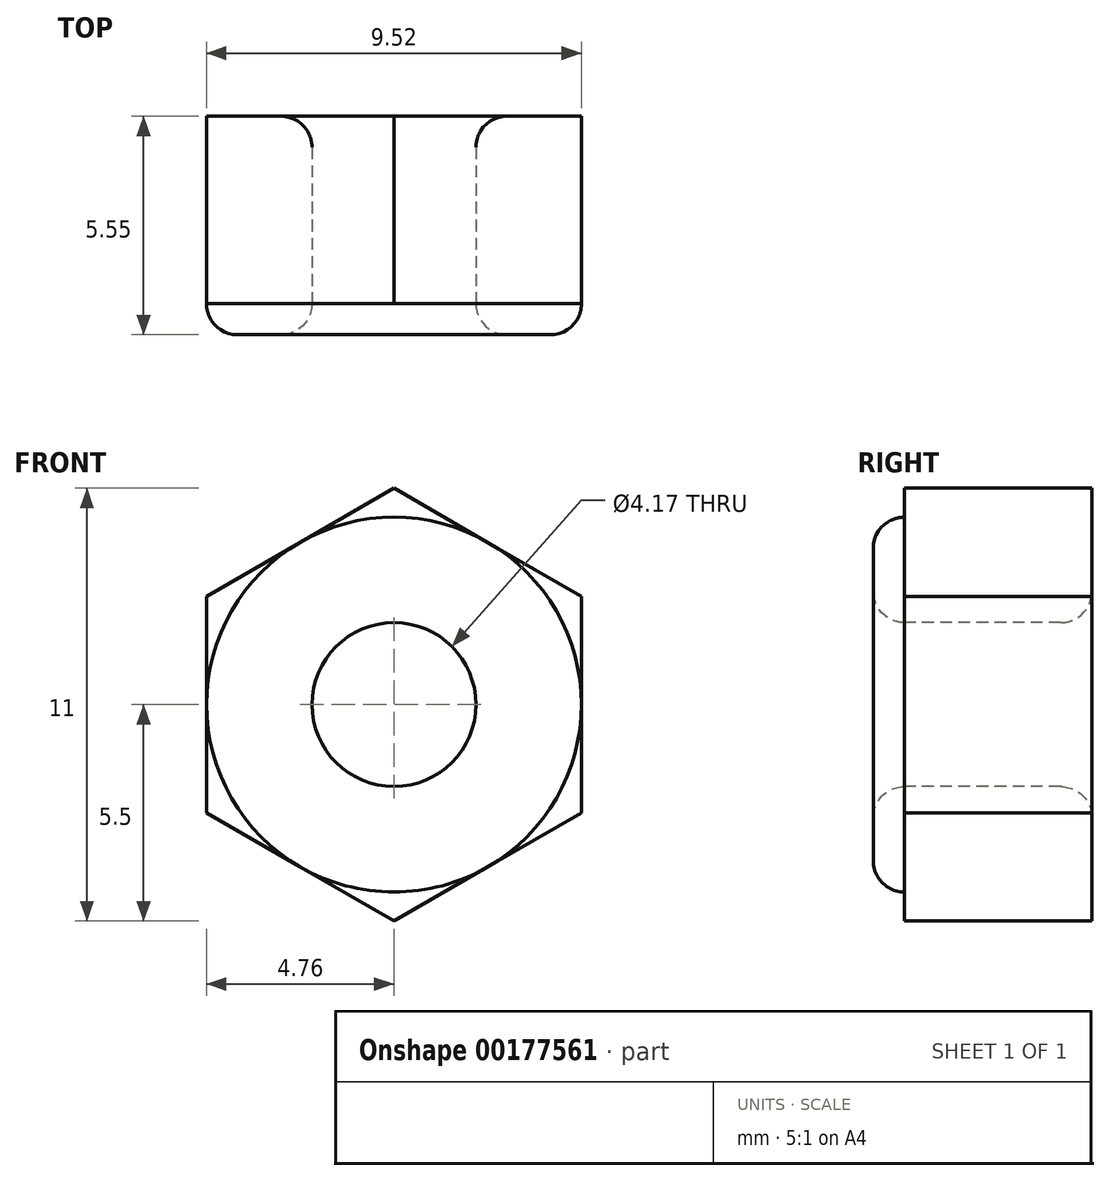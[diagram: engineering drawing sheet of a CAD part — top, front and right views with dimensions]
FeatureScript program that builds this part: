
annotation { "Feature Type Name" : "Feature", "Feature Type Description" : "" }
export const myFeature = defineFeature(function(context is Context, id is Id, definition is map)
    precondition{}
    {
        {
            var Q0;
            Q0=qCreatedBy(makeId("Front.planeOp"),FACE);
            var sketch = newSketch(context, id + "F0", { "sketchPlane" : qUnion([Q0])});
            skCircle(sketch, "E0.cCircle", {"center": v(0, 0) * mm, "radius": 4.76 * mm, "construction": true});
            skLineSegment(sketch, "E0.0", {"start": v(4.76, 2.75) * mm, "end": v(4.76, -2.75) * mm});
            skLineSegment(sketch, "E0.1", {"start": v(4.76, -2.75) * mm, "end": v(0, -5.5) * mm});
            skLineSegment(sketch, "E0.2", {"start": v(0, -5.5) * mm, "end": v(-4.76, -2.75) * mm});
            skLineSegment(sketch, "E0.3", {"start": v(-4.76, -2.75) * mm, "end": v(-4.76, 2.75) * mm});
            skLineSegment(sketch, "E0.4", {"start": v(-4.76, 2.75) * mm, "end": v(0, 5.5) * mm});
            skLineSegment(sketch, "E0.5", {"start": v(0, 5.5) * mm, "end": v(4.76, 2.75) * mm});
            skPoint(sketch, "E0.0.midPoint", {"position": v(4.76, 0) * mm});
            skCircle(sketch, "E1", {"center": v(0, 0) * mm, "radius": 2.08 * mm});
            skSolve(sketch);
        }
        {
            var Q0;
            Q0 = qSketchRegion(id + "F0", true);
            extrude(context, id + "F1", {"entities" : qUnion([Q0]), "oppositeDirection" : true, "depth" : 4.76 * mm});
        }
        {
            var Q0;
            Q0=makeQuery(id+"F1.opExtrude","CAP_FACE",FACE,{"disambiguationData":[OSD([sQuery(id+"F0.wireOp",EDGE,"E0.0"),sQuery(id+"F0.wireOp",EDGE,"E0.1"),sQuery(id+"F0.wireOp",EDGE,"E0.2"),sQuery(id+"F0.wireOp",EDGE,"E0.3"),sQuery(id+"F0.wireOp",EDGE,"E0.4"),sQuery(id+"F0.wireOp",EDGE,"E0.5"),sQuery(id+"F0.wireOp",EDGE,"E1")])],"isStart":true});
            var sketch = newSketch(context, id + "F2", { "sketchPlane" : qUnion([Q0])});
            skCircle(sketch, "E2", {"center": v(0, 0) * mm, "radius": 2.08 * mm});
            skCircle(sketch, "E3", {"center": v(0, 0) * mm, "radius": 4.76 * mm});
            skSolve(sketch);
        }
        {
            var Q0;
            Q0 = qSketchRegion(id + "F2", true);
            extrude(context, id + "F3", {"entities" : qUnion([Q0]), "operationType" : NewBodyOperationType.ADD, "depth" : 0.8 * mm});
        }
        {
            var Q0;
            Q0=makeQuery(id+"F3.opExtrude","CAP_EDGE",EDGE,{"disambiguationData":[OSD([sQuery(id+"F2.wireOp",EDGE,"E3")])],"isStart":false});
            var Q1;
            Q1=makeQuery(id+"F3.opExtrude","CAP_EDGE",EDGE,{"disambiguationData":[OSD([sQuery(id+"F2.wireOp",EDGE,"E2")])],"isStart":false});
            fillet(context, id + "F4", {"entities" : qUnion([Q0, Q1]), "radius" : 0.8 * mm, "tangentPropagation" : true, "allowEdgeOverflow" : false});
        }
        {
            var Q0;
            Q0=makeQuery(id+"F1.opExtrude","CAP_EDGE",EDGE,{"disambiguationData":[OSD([sQuery(id+"F0.wireOp",EDGE,"E1")])],"isStart":false});
            fillet(context, id + "F5", {"entities" : qUnion([Q0]), "radius" : 0.8 * mm, "tangentPropagation" : true, "allowEdgeOverflow" : false});
        }
    });
